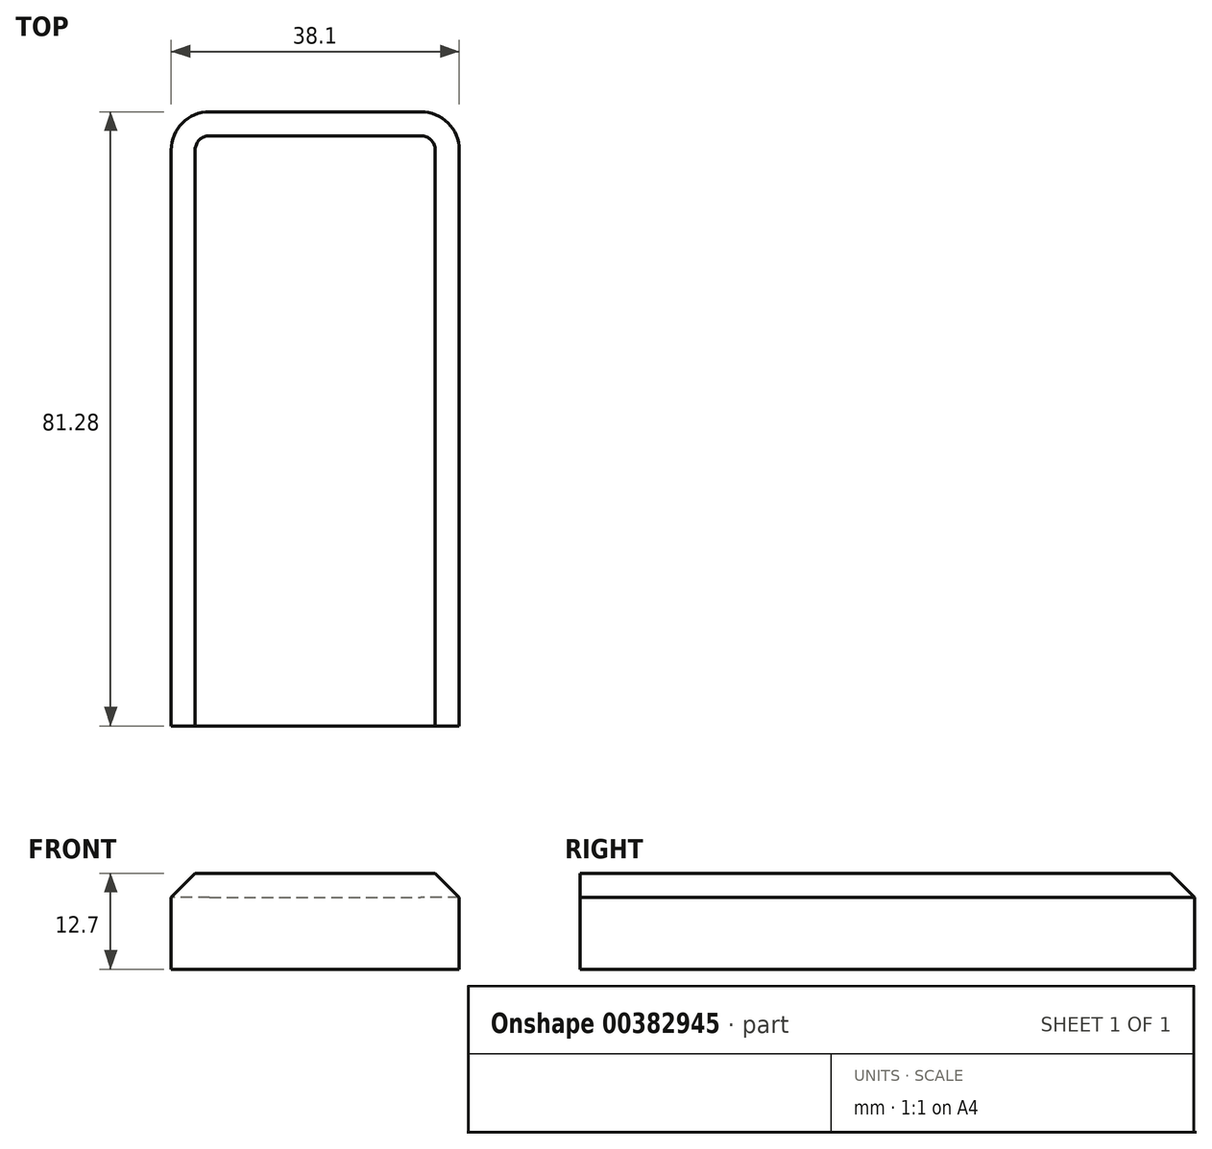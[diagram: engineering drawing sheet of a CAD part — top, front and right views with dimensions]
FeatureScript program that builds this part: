
annotation { "Feature Type Name" : "Feature", "Feature Type Description" : "" }
export const myFeature = defineFeature(function(context is Context, id is Id, definition is map)
    precondition{}
    {
        {
            var Q0;
            Q0=qCreatedBy(makeId("Top.planeOp"),FACE);
            var sketch = newSketch(context, id + "F0", { "sketchPlane" : qUnion([Q0])});
            skLineSegment(sketch, "E0.bottom", {"start": v(19.05, 40.64) * mm, "end": v(-19.05, 40.64) * mm});
            skLineSegment(sketch, "E0.top", {"start": v(19.05, -40.64) * mm, "end": v(-19.05, -40.64) * mm});
            skLineSegment(sketch, "E0.left", {"start": v(19.05, 40.64) * mm, "end": v(19.05, -40.64) * mm});
            skLineSegment(sketch, "E0.right", {"start": v(-19.05, 40.64) * mm, "end": v(-19.05, -40.64) * mm});
            skPoint(sketch, "E0.middle", {"position": v(0, 0) * mm});
            skSolve(sketch);
        }
        {
            var Q0;
            Q0=makeQuery(id+"F0.imprint","IMPRINT",FACE,{"disambiguationData":[TD([[makeQuery(id+"F0.imprint","IMPRINT",EDGE,{"derivedFrom":sQuery(id+"F0.wireOp",EDGE,"E0.bottom")}),1.0]])]});
            extrude(context, id + "F1", {"entities" : qUnion([Q0]), "depth" : 12.7 * mm});
        }
        {
            var Q0;
            Q0=makeQuery(id+"F1.opExtrude","SWEPT_EDGE",EDGE,{"disambiguationData":[OSD([sQuery(id+"F0.wireOp",EDGE,"E0.bottom"),sQuery(id+"F0.wireOp",EDGE,"E0.right")])]});
            var Q1;
            Q1=makeQuery(id+"F1.opExtrude","SWEPT_EDGE",EDGE,{"disambiguationData":[OSD([sQuery(id+"F0.wireOp",EDGE,"E0.bottom"),sQuery(id+"F0.wireOp",EDGE,"E0.left")])]});
            fillet(context, id + "F2", {"entities" : qUnion([Q0, Q1]), "radius" : 5.08 * mm, "tangentPropagation" : true, "allowEdgeOverflow" : false});
        }
        {
            var Q0;
            Q0=makeQuery(id+"F1.opExtrude","CAP_EDGE",EDGE,{"disambiguationData":[OSD([sQuery(id+"F0.wireOp",EDGE,"E0.right")])],"isStart":false});
            var Q1;
            Q1=makeQuery(id+"F1.opExtrude","CAP_EDGE",EDGE,{"disambiguationData":[OSD([sQuery(id+"F0.wireOp",EDGE,"E0.bottom")])],"isStart":false});
            var Q2;
            Q2=makeQuery(id+"F1.opExtrude","CAP_EDGE",EDGE,{"disambiguationData":[OSD([sQuery(id+"F0.wireOp",EDGE,"E0.left")])],"isStart":false});
            chamfer(context, id + "F3", {"entities" : qUnion([Q0, Q1, Q2]), "width" : 3.17 * mm, "tangentPropagation" : true});
        }
    });
